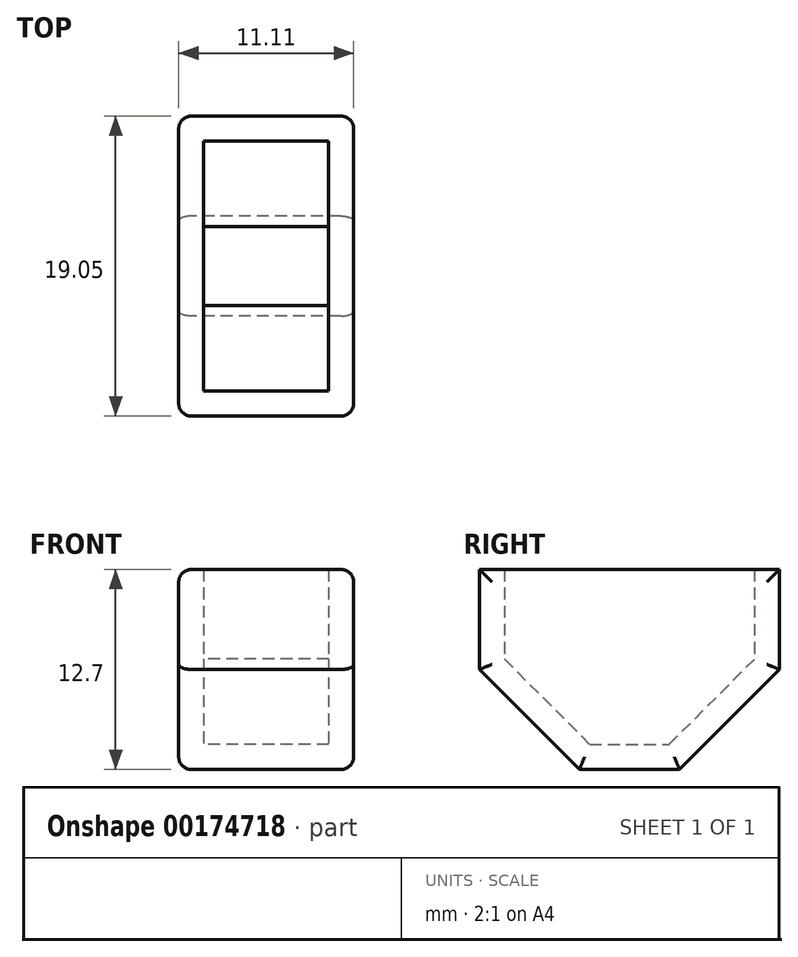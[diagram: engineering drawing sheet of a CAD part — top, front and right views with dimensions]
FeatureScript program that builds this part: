
annotation { "Feature Type Name" : "Feature", "Feature Type Description" : "" }
export const myFeature = defineFeature(function(context is Context, id is Id, definition is map)
    precondition{}
    {
        {
            var Q0;
            Q0=qCreatedBy(makeId("Right.planeOp"),FACE);
            var sketch = newSketch(context, id + "F0", { "sketchPlane" : qUnion([Q0])});
            skLineSegment(sketch, "E0", {"start": v(-3.74, 55.92) * mm, "end": v(-3.74, -96.48) * mm, "construction": true});
            skPoint(sketch, "E1", {"position": v(-13.27, 55.92) * mm});
            skPoint(sketch, "E2", {"position": v(-8.5, 55.92) * mm});
            skCircle(sketch, "E3", {"center": v(-8.5, 44.8) * mm, "radius": 11.11 * mm});
            skCircle(sketch, "E4", {"center": v(-8.5, 44.8) * mm, "radius": 9.53 * mm});
            skLineSegment(sketch, "E5", {"start": v(-8.5, 33.7) * mm, "end": v(-3.74, 33.7) * mm});
            skLineSegment(sketch, "E6", {"start": v(-8.5, 55.92) * mm, "end": v(-8.5, -96.48) * mm, "construction": true});
            skPoint(sketch, "E7", {"position": v(-3.74, 14.64) * mm});
            skLineSegment(sketch, "E8", {"start": v(-3.74, 24.17) * mm, "end": v(-2.16, 24.17) * mm, "construction": true});
            skArc(sketch, "E9", {"start": v(-3.74, 14.64) * mm, "mid": v(-2.16, 24.17) * mm, "end": v(-3.74, 33.7) * mm});
            skLineSegment(sketch, "E10", {"start": v(-3.74, 14.64) * mm, "end": v(15.3, 14.64) * mm, "construction": true});
            skArc(sketch, "E11.MirrorCS", {"start": v(-3.74, 14.64) * mm, "mid": v(-2.16, 5.12) * mm, "end": v(-3.74, -4.4) * mm});
            skLineSegment(sketch, "E12", {"start": v(-3.74, -4.4) * mm, "end": v(15.3, -4.4) * mm, "construction": true});
            skArc(sketch, "E13.MirrorCS", {"start": v(-3.74, -23.46) * mm, "mid": v(-2.16, -13.93) * mm, "end": v(-3.74, -4.4) * mm});
            skLineSegment(sketch, "E14", {"start": v(-3.74, -23.46) * mm, "end": v(15.3, -23.46) * mm, "construction": true});
            skArc(sketch, "E15.MirrorCS", {"start": v(-3.74, -23.46) * mm, "mid": v(-2.16, -32.98) * mm, "end": v(-3.74, -42.5) * mm});
            skLineSegment(sketch, "E16", {"start": v(-3.74, -42.5) * mm, "end": v(-3.74, -48.86) * mm});
            skLineSegment(sketch, "E17", {"start": v(-3.74, -55.2) * mm, "end": v(2.6, -55.2) * mm, "construction": true});
            skLineSegment(sketch, "E18", {"start": v(-3.74, -48.86) * mm, "end": v(2.6, -55.2) * mm});
            skLineSegment(sketch, "E19", {"start": v(2.6, -55.2) * mm, "end": v(8.96, -55.2) * mm});
            skLineSegment(sketch, "E20", {"start": v(8.96, -55.2) * mm, "end": v(15.3, -48.86) * mm});
            skLineSegment(sketch, "E21", {"start": v(15.3, 55.92) * mm, "end": v(15.3, -48.86) * mm});
            skLineSegment(sketch, "E22", {"start": v(-3.74, 33.7) * mm, "end": v(15.3, 33.7) * mm, "construction": true});
            skPoint(sketch, "E23", {"position": v(5.78, 33.7) * mm});
            skPoint(sketch, "E24", {"position": v(5.78, 14.64) * mm});
            skPoint(sketch, "E25", {"position": v(5.78, -4.4) * mm});
            skPoint(sketch, "E26", {"position": v(5.78, -23.46) * mm});
            skLineSegment(sketch, "E27", {"start": v(-3.74, -42.5) * mm, "end": v(15.3, -42.5) * mm});
            skSolve(sketch);
        }
        {
            var Q0;
            Q0=makeQuery(id+"F0.imprint","IMPRINT",FACE,{"disambiguationData":[TD([[makeQuery(id+"F0.imprint","IMPRINT",EDGE,{"derivedFrom":sQuery(id+"F0.wireOp",EDGE,"E16")}),1.0]])]});
            extrude(context, id + "F1", {"entities" : qUnion([Q0]), "depth" : 11.1 * mm});
        }
        {
            var Q0;
            Q0=makeQuery(id+"F1.opExtrude","SWEPT_FACE",FACE,{"disambiguationData":[OSD([sQuery(id+"F0.wireOp",EDGE,"E27")])]});
            shell(context, id + "F2", {"entities" : qUnion([Q0]), "thickness" : 1.59 * mm});
        }
        {
            var Q0;
            Q0=makeQuery(id+"F1.opExtrude","CAP_FACE",FACE,{"disambiguationData":[OSD([sQuery(id+"F0.wireOp",EDGE,"E16"),sQuery(id+"F0.wireOp",EDGE,"E18"),sQuery(id+"F0.wireOp",EDGE,"E19"),sQuery(id+"F0.wireOp",EDGE,"E20"),sQuery(id+"F0.wireOp",EDGE,"E21"),sQuery(id+"F0.wireOp",EDGE,"E27")])],"isStart":false});
            var Q1;
            Q1=makeQuery(id+"F1.opExtrude","CAP_FACE",FACE,{"disambiguationData":[OSD([sQuery(id+"F0.wireOp",EDGE,"E16"),sQuery(id+"F0.wireOp",EDGE,"E18"),sQuery(id+"F0.wireOp",EDGE,"E19"),sQuery(id+"F0.wireOp",EDGE,"E20"),sQuery(id+"F0.wireOp",EDGE,"E21"),sQuery(id+"F0.wireOp",EDGE,"E27")])],"isStart":true});
            fillet(context, id + "F3", {"entities" : qUnion([Q0, Q1]), "radius" : 0.8 * mm, "tangentPropagation" : true, "allowEdgeOverflow" : false});
        }
    });
